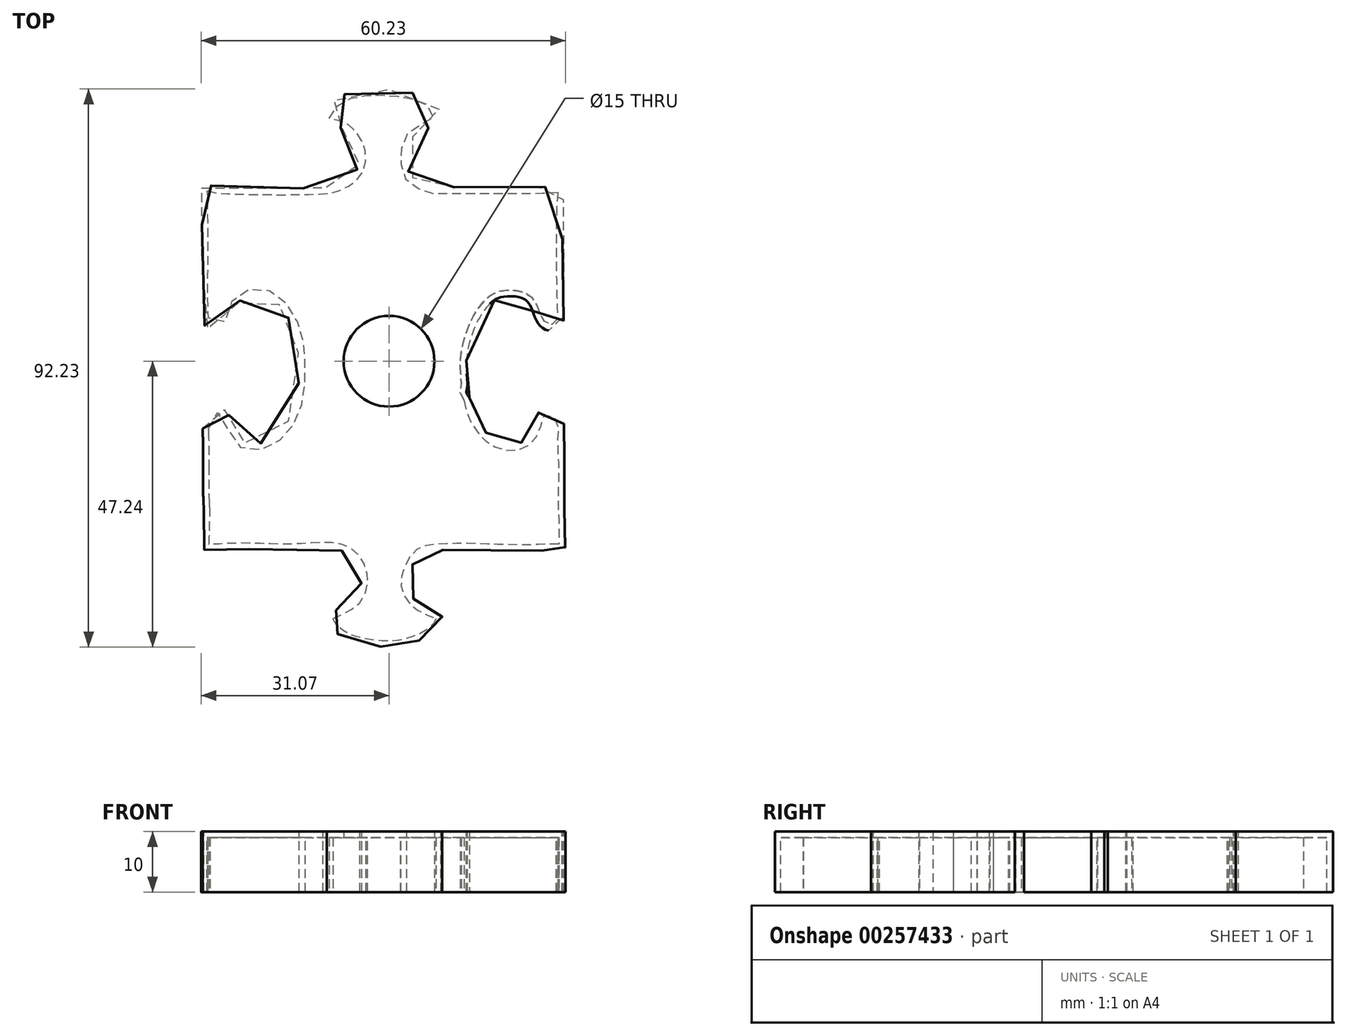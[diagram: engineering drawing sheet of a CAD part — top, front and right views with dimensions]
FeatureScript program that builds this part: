
annotation { "Feature Type Name" : "Feature", "Feature Type Description" : "" }
export const myFeature = defineFeature(function(context is Context, id is Id, definition is map)
    precondition{}
    {
        {
            var Q0;
            Q0=qCreatedBy(makeId("Top.planeOp"),FACE);
            var sketch = newSketch(context, id + "F0", { "sketchPlane" : qUnion([Q0])});
            skFitSpline(sketch, "E0", {"points": [v(-30.6, -24.54) * mm, v(-30.73, -21.1) * mm, v(-30.73, -17.76) * mm, v(-30.73, -13.08) * mm, v(-30.73, -10.25) * mm, v(-29.5, -7.66) * mm, v(-27.77, -7.66) * mm, v(-26.17, -9.5) * mm, v(-25.06, -12.34) * mm, v(-23.21, -13.7) * mm, v(-19.27, -12.71) * mm, v(-15.45, -7.16) * mm, v(-14.96, 1.34) * mm, v(-15.57, 4.92) * mm, v(-18.65, 9.85) * mm, v(-22.23, 10.95) * mm, v(-25.06, 9.48) * mm, v(-26.42, 5.78) * mm, v(-29.87, 5.28) * mm, v(-30.98, 10.34) * mm, v(-30.98, 25.75) * mm, v(-30.98, 28.46) * mm, v(-30.36, 29.32) * mm, v(-29.5, 29.07) * mm, v(-27.4, 28.7) * mm, v(-12.5, 28.58) * mm, v(-8.42, 29.2) * mm, v(-5.59, 31.17) * mm, v(-4.83, 33.95) * mm, v(-5.82, 36.73) * mm, v(-8.24, 38.7) * mm, v(-10.85, 39.6) * mm, v(-9.23, 42.93) * mm, v(-4.65, 44.81) * mm, v(1.36, 44.81) * mm, v(6.75, 43.2) * mm, v(8.54, 40.41) * mm, v(5.94, 38.26) * mm, v(3.51, 36.56) * mm, v(2.98, 32.43) * mm, v(3.78, 30.45) * mm, v(6.57, 28.93) * mm, v(9.7, 28.75) * mm, v(22.81, 28.75) * mm, v(26.58, 28.84) * mm, v(28.82, 28.84) * mm, v(28.82, 27.31) * mm, v(28.91, 7.2) * mm, v(29, 7.74) * mm, v(28.82, 6.67) * mm, v(26.76, 5.05) * mm, v(24.7, 6.13) * mm, v(23.7, 8.37) * mm, v(22.36, 10.26) * mm, v(19.31, 10.7) * mm, v(17.34, 10.08) * mm, v(14.73, 6.85) * mm, v(12.76, 0) * mm, v(12.94, -4.1) * mm, v(12.75, -5.02) * mm, v(12.76, -5.18) * mm, v(12.8, -5.27) * mm, v(13.3, -6.07) * mm], "startDerivative": vector(-9.33, 218.17) * mm, "endDerivative": vector(84.68, -99.58) * mm});
            skFitSpline(sketch, "E1", {"points": [v(13.3, -6.07) * mm, v(14.09, -8.9) * mm, v(16.45, -12.26) * mm, v(19.65, -13.78) * mm, v(22.68, -12.94) * mm, v(24.2, -10.24) * mm, v(25.04, -8.05) * mm, v(27.32, -7.88) * mm, v(29, -11) * mm, v(28.84, -12.94) * mm, v(29, -16.98) * mm, v(28.92, -23.13) * mm, v(29.09, -26.84) * mm, v(29.09, -30.55) * mm, v(29.09, -31.3) * mm, v(27.83, -31.22) * mm, v(25.04, -31.3) * mm, v(19.06, -31.3) * mm, v(13.3, -31.14) * mm, v(8.27, -31.22) * mm, v(5.24, -31.9) * mm, v(3.64, -34) * mm, v(2.97, -36.87) * mm, v(4.48, -39.73) * mm, v(7.6, -41.42) * mm, v(8.78, -42.26) * mm, v(7.68, -44.45) * mm, v(5.07, -46.14) * mm, v(1.95, -47.06) * mm, v(-2.1, -47.15) * mm, v(-7.06, -45.97) * mm, v(-9.67, -43.86) * mm, v(-10.18, -42.1) * mm, v(-7.57, -40.66) * mm, v(-5.04, -38.47) * mm, v(-4.7, -34.85) * mm, v(-6.9, -31.73) * mm, v(-10.85, -30.97) * mm, v(-16, -31.22) * mm, v(-21.22, -31.14) * mm, v(-27.03, -31.14) * mm, v(-30.57, -31.14) * mm, v(-30.74, -30.13) * mm, v(-30.6, -24.54) * mm, v(-30.66, -23.37) * mm, v(-30.73, -21.1) * mm, v(-30.73, -17.76) * mm, v(-30.81, -11.15) * mm], "startDerivative": vector(27.25, -137.77) * mm, "endDerivative": vector(-2.86, 239.91) * mm});
            skSolve(sketch);
        }
        {
            var Q0;
            {var subQ0=sQuery(id+"F0.wireOp",EDGE,"E1");var subQ1=sQuery(id+"F0.wireOp",EDGE,"E0");var subQ7=makeQuery(id+"F0.imprint","INTERSECT",VERTEX,{"disambiguationData":[OD(3.0)],"derivedFrom":[subQ1,subQ0]});Q0=makeQuery(id+"F0.imprint","IMPRINT",FACE,{"disambiguationData":[TD([[makeQuery(id+"F0.imprint","IMPRINT",EDGE,{"disambiguationData":[TD([[subQ7,-1.0]])],"derivedFrom":subQ1}),-1.0]])]});}
            extrude(context, id + "F1", {"entities" : qUnion([Q0]), "depth" : 10 * mm});
        }
        {
            var Q0;
            Q0=makeQuery(id+"F1.opExtrude","CAP_FACE",FACE,{"disambiguationData":[OSD([sQuery(id+"F0.wireOp",EDGE,"E0"),sQuery(id+"F0.wireOp",EDGE,"E1")])],"isStart":true});
            shell(context, id + "F2", {"entities" : qUnion([Q0]), "thickness" : 1 * mm});
        }
        {
            var Q0;
            Q0=makeQuery(id+"F2.opShell","OFFSET_FACE",FACE,{"disambiguationData":[OSD([sQuery(id+"F0.wireOp",EDGE,"E0"),sQuery(id+"F0.wireOp",EDGE,"E1")])]});
            var sketch = newSketch(context, id + "F3", { "sketchPlane" : qUnion([Q0])});
            skCircle(sketch, "E2", {"center": v(0, 0) * mm, "radius": 7.5 * mm});
            skSolve(sketch);
        }
        {
            var Q0;
            Q0 = qSketchRegion(id + "F3", true);
            extrude(context, id + "F4", {"entities" : qUnion([Q0]), "operationType" : NewBodyOperationType.REMOVE, "oppositeDirection" : true, "depth" : 25 * mm});
        }
    });
